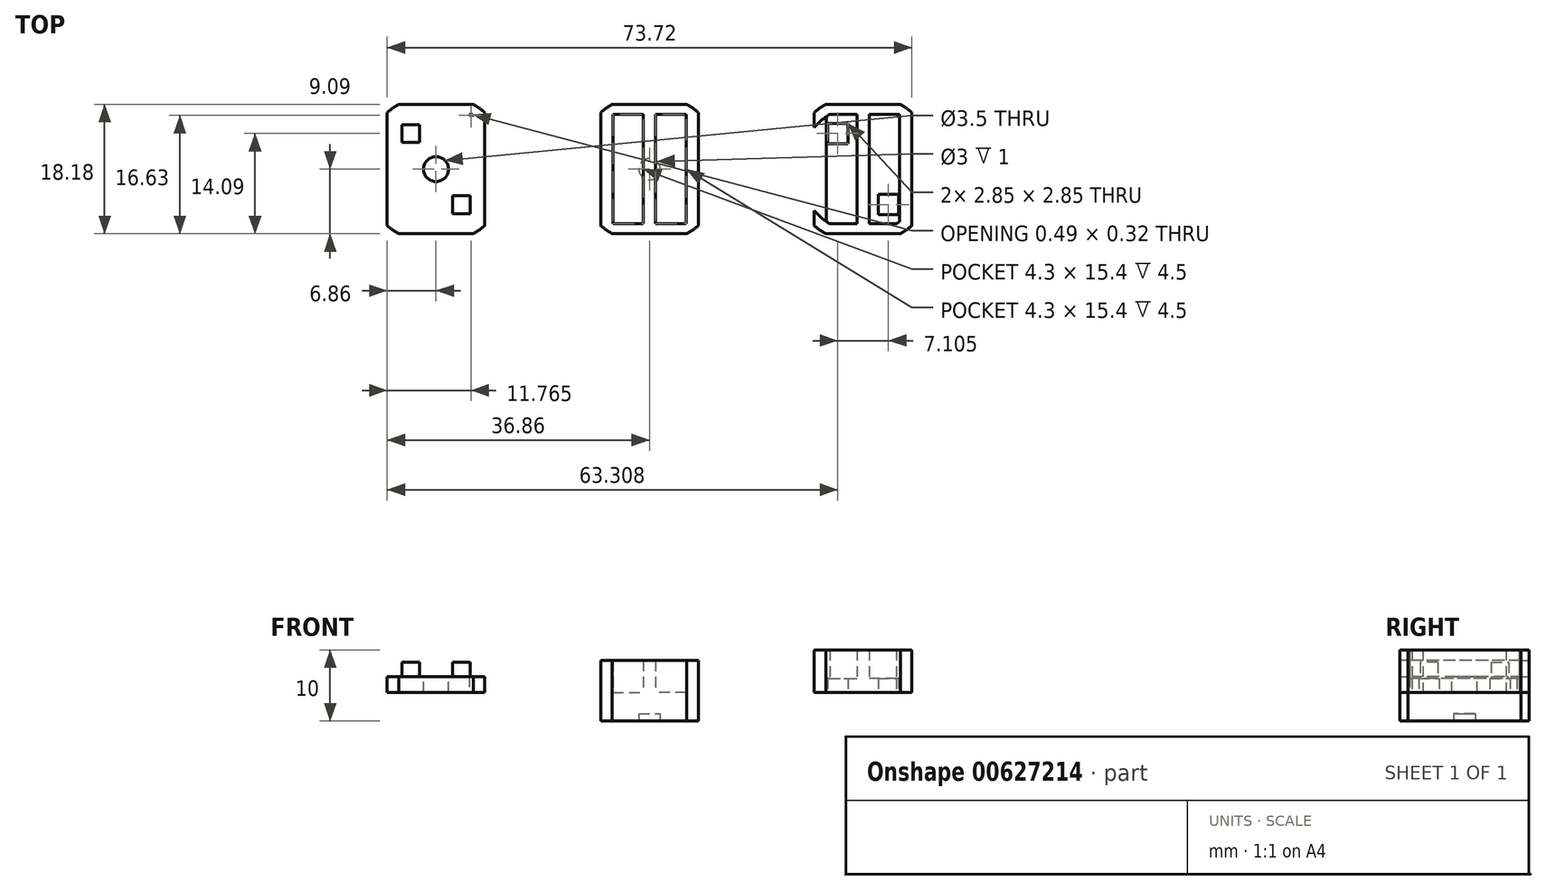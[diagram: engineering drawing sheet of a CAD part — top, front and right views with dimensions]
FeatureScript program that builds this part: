
annotation { "Feature Type Name" : "Feature", "Feature Type Description" : "" }
export const myFeature = defineFeature(function(context is Context, id is Id, definition is map)
    precondition{}
    {
        {
            var Q0;
            Q0=qCreatedBy(makeId("Top.planeOp"),FACE);
            var sketch = newSketch(context, id + "F0", { "sketchPlane" : qUnion([Q0])});
            skCircle(sketch, "E0", {"center": v(0, 0) * mm, "radius": 10.5 * mm});
            skCircle(sketch, "E1", {"center": v(0, 0) * mm, "radius": 9 * mm});
            skLineSegment(sketch, "E2.bottom", {"start": v(-5.15, 7.7) * mm, "end": v(-0.85, 7.7) * mm});
            skLineSegment(sketch, "E2.top", {"start": v(-5.15, -7.7) * mm, "end": v(-0.85, -7.7) * mm});
            skLineSegment(sketch, "E2.left", {"start": v(-5.15, 7.7) * mm, "end": v(-5.15, -7.7) * mm});
            skLineSegment(sketch, "E2.right", {"start": v(-0.85, 7.7) * mm, "end": v(-0.85, -7.7) * mm});
            skPoint(sketch, "E2.middle", {"position": v(-3, 0) * mm});
            skLineSegment(sketch, "E3.MirrorCS", {"start": v(0.85, 7.7) * mm, "end": v(0.85, -7.7) * mm});
            skLineSegment(sketch, "E4.MirrorCS", {"start": v(5.15, 7.7) * mm, "end": v(0.85, 7.7) * mm});
            skLineSegment(sketch, "E5.MirrorCS", {"start": v(5.15, 7.7) * mm, "end": v(5.15, -7.7) * mm});
            skLineSegment(sketch, "E6.MirrorCS", {"start": v(5.15, -7.7) * mm, "end": v(0.85, -7.7) * mm});
            skLineSegment(sketch, "E7", {"start": v(-6.86, 7.95) * mm, "end": v(-6.86, -7.95) * mm});
            skLineSegment(sketch, "E8", {"start": v(-5.25, -9.1) * mm, "end": v(5.25, -9.1) * mm});
            skLineSegment(sketch, "E9.MirrorCS", {"start": v(6.86, 7.95) * mm, "end": v(6.86, -7.95) * mm});
            skLineSegment(sketch, "E10.MirrorCS", {"start": v(5.25, -9.1) * mm, "end": v(-5.25, -9.1) * mm});
            skLineSegment(sketch, "E11.MirrorCS", {"start": v(5.25, 9.1) * mm, "end": v(-5.25, 9.1) * mm});
            skLineSegment(sketch, "E12", {"start": v(-15, 7.95) * mm, "end": v(-15, -7.95) * mm, "construction": true});
            skLineSegment(sketch, "E13", {"start": v(15, 7.95) * mm, "end": v(15, -7.95) * mm, "construction": true});
            skLineSegment(sketch, "E14.MirrorCS", {"start": v(35.25, -9.1) * mm, "end": v(24.75, -9.1) * mm});
            skLineSegment(sketch, "E15.MirrorCS", {"start": v(24.75, -9.1) * mm, "end": v(35.25, -9.1) * mm});
            skLineSegment(sketch, "E16.MirrorCS", {"start": v(30.85, 7.7) * mm, "end": v(30.85, -7.7) * mm});
            skLineSegment(sketch, "E17.MirrorCS", {"start": v(35.15, -7.7) * mm, "end": v(30.85, -7.7) * mm});
            skLineSegment(sketch, "E18.MirrorCS", {"start": v(29.15, 7.7) * mm, "end": v(29.15, -7.7) * mm});
            skLineSegment(sketch, "E19.MirrorCS", {"start": v(36.86, 7.95) * mm, "end": v(36.86, -7.95) * mm});
            skCircle(sketch, "E20.MirrorC", {"center": v(30, 0) * mm, "radius": 10.5 * mm});
            skLineSegment(sketch, "E21.MirrorCS", {"start": v(24.85, 7.7) * mm, "end": v(29.15, 7.7) * mm});
            skCircle(sketch, "E22.MirrorC", {"center": v(30, 0) * mm, "radius": 9 * mm});
            skLineSegment(sketch, "E23.MirrorCS", {"start": v(24.85, 7.7) * mm, "end": v(24.85, -7.7) * mm});
            skLineSegment(sketch, "E24.MirrorCS", {"start": v(35.15, 7.7) * mm, "end": v(35.15, -7.7) * mm});
            skPoint(sketch, "E25.MirrorP", {"position": v(33, 0) * mm});
            skLineSegment(sketch, "E26.MirrorCS", {"start": v(24.75, 9.1) * mm, "end": v(35.25, 9.1) * mm});
            skLineSegment(sketch, "E27.MirrorCS", {"start": v(23.14, 7.95) * mm, "end": v(23.14, -7.95) * mm});
            skLineSegment(sketch, "E28.MirrorCS", {"start": v(35.15, 7.7) * mm, "end": v(30.85, 7.7) * mm});
            skLineSegment(sketch, "E29.MirrorCS", {"start": v(24.85, -7.7) * mm, "end": v(29.15, -7.7) * mm});
            skLineSegment(sketch, "E30.MirrorCS", {"start": v(-24.75, -9.1) * mm, "end": v(-35.25, -9.1) * mm});
            skLineSegment(sketch, "E31.MirrorCS", {"start": v(-35.15, 7.7) * mm, "end": v(-35.15, -7.7) * mm});
            skLineSegment(sketch, "E32.MirrorCS", {"start": v(-30.85, 7.7) * mm, "end": v(-30.85, -7.7) * mm});
            skCircle(sketch, "E33.MirrorC", {"center": v(-30, 0) * mm, "radius": 10.5 * mm});
            skLineSegment(sketch, "E34.MirrorCS", {"start": v(-24.85, -7.7) * mm, "end": v(-29.15, -7.7) * mm});
            skCircle(sketch, "E35.MirrorC", {"center": v(-30, 0) * mm, "radius": 9 * mm});
            skLineSegment(sketch, "E36.MirrorCS", {"start": v(-35.15, 7.7) * mm, "end": v(-30.85, 7.7) * mm});
            skLineSegment(sketch, "E37.MirrorCS", {"start": v(-24.85, 7.7) * mm, "end": v(-24.85, -7.7) * mm});
            skLineSegment(sketch, "E38.MirrorCS", {"start": v(-24.85, 7.7) * mm, "end": v(-29.15, 7.7) * mm});
            skLineSegment(sketch, "E39.MirrorCS", {"start": v(-29.15, 7.7) * mm, "end": v(-29.15, -7.7) * mm});
            skLineSegment(sketch, "E40.MirrorCS", {"start": v(-35.25, 9.1) * mm, "end": v(-24.75, 9.1) * mm});
            skLineSegment(sketch, "E41.MirrorCS", {"start": v(-35.25, -9.1) * mm, "end": v(-24.75, -9.1) * mm});
            skLineSegment(sketch, "E42.MirrorCS", {"start": v(-36.86, 7.95) * mm, "end": v(-36.86, -7.95) * mm});
            skLineSegment(sketch, "E43.MirrorCS", {"start": v(-23.14, 7.95) * mm, "end": v(-23.14, -7.95) * mm});
            skPoint(sketch, "E44.MirrorP", {"position": v(-27, 0) * mm});
            skLineSegment(sketch, "E45.MirrorCS", {"start": v(-35.15, -7.7) * mm, "end": v(-30.85, -7.7) * mm});
            skSolve(sketch);
        }
        {
            var Q0;
            {var subQ0=sQuery(id+"F0.wireOp",EDGE,"E5.MirrorCS");var subQ1=sQuery(id+"F0.wireOp",EDGE,"E1");var subQ2=makeQuery(id+"F0.imprint","INTERSECT",VERTEX,{"disambiguationData":[OD(0.0)],"derivedFrom":[subQ1,subQ0]});Q0=makeQuery(id+"F0.imprint","IMPRINT",FACE,{"disambiguationData":[TD([[makeQuery(id+"F0.imprint","IMPRINT",EDGE,{"disambiguationData":[TD([[subQ2,1.0]])],"derivedFrom":subQ1}),1.0]])]});}
            var Q1;
            {var subQ9=sQuery(id+"F0.wireOp",EDGE,"E11.MirrorCS");Q1=makeQuery(id+"F0.imprint","IMPRINT",FACE,{"disambiguationData":[TD([[makeQuery(id+"F0.imprint","IMPRINT",EDGE,{"derivedFrom":subQ9}),1.0]])]});}
            var Q2;
            {var subQ3=sQuery(id+"F0.wireOp",EDGE,"E2.right");Q2=makeQuery(id+"F0.imprint","IMPRINT",FACE,{"disambiguationData":[TD([[makeQuery(id+"F0.imprint","IMPRINT",EDGE,{"derivedFrom":subQ3}),1.0]])]});}
            var Q3;
            {var subQ0=sQuery(id+"F0.wireOp",EDGE,"E2.left");var subQ1=sQuery(id+"F0.wireOp",EDGE,"E1");var subQ2=makeQuery(id+"F0.imprint","INTERSECT",VERTEX,{"disambiguationData":[OD(0.0)],"derivedFrom":[subQ1,subQ0]});Q3=makeQuery(id+"F0.imprint","IMPRINT",FACE,{"disambiguationData":[TD([[makeQuery(id+"F0.imprint","IMPRINT",EDGE,{"disambiguationData":[TD([[subQ2,-1.0]])],"derivedFrom":subQ1}),1.0]])]});}
            var Q4;
            {var subQ17=sQuery(id+"F0.wireOp",EDGE,"E8");Q4=makeQuery(id+"F0.imprint","IMPRINT",FACE,{"disambiguationData":[TD([[makeQuery(id+"F0.imprint","IMPRINT",EDGE,{"derivedFrom":subQ17}),1.0]])]});}
            extrude(context, id + "F1", {"entities" : qUnion([Q0, Q1, Q2, Q3, Q4]), "depth" : 4.5 * mm, "offsetDistance" : 25 * mm});
        }
        {
            var Q0;
            {var subQ0=sQuery(id+"F0.wireOp",EDGE,"E3.MirrorCS");Q0=makeQuery(id+"F0.imprint","IMPRINT",FACE,{"disambiguationData":[TD([[makeQuery(id+"F0.imprint","IMPRINT",EDGE,{"derivedFrom":subQ0}),1.0]])]});}
            var Q1;
            {var subQ3=sQuery(id+"F0.wireOp",EDGE,"E2.right");Q1=makeQuery(id+"F0.imprint","IMPRINT",FACE,{"disambiguationData":[TD([[makeQuery(id+"F0.imprint","IMPRINT",EDGE,{"derivedFrom":subQ3}),-1.0]])]});}
            var Q2;
            {var subQ3=sQuery(id+"F0.wireOp",EDGE,"E2.right");Q2=makeQuery(id+"F0.imprint","IMPRINT",FACE,{"disambiguationData":[TD([[makeQuery(id+"F0.imprint","IMPRINT",EDGE,{"derivedFrom":subQ3}),1.0]])]});}
            var Q3;
            {var subQ9=sQuery(id+"F0.wireOp",EDGE,"E11.MirrorCS");Q3=makeQuery(id+"F0.imprint","IMPRINT",FACE,{"disambiguationData":[TD([[makeQuery(id+"F0.imprint","IMPRINT",EDGE,{"derivedFrom":subQ9}),1.0]])]});}
            var Q4;
            {var subQ0=sQuery(id+"F0.wireOp",EDGE,"E5.MirrorCS");var subQ1=sQuery(id+"F0.wireOp",EDGE,"E1");var subQ2=makeQuery(id+"F0.imprint","INTERSECT",VERTEX,{"disambiguationData":[OD(0.0)],"derivedFrom":[subQ1,subQ0]});Q4=makeQuery(id+"F0.imprint","IMPRINT",FACE,{"disambiguationData":[TD([[makeQuery(id+"F0.imprint","IMPRINT",EDGE,{"disambiguationData":[TD([[subQ2,1.0]])],"derivedFrom":subQ1}),1.0]])]});}
            var Q5;
            {var subQ0=sQuery(id+"F0.wireOp",EDGE,"E4.MirrorCS");var subQ1=sQuery(id+"F0.wireOp",EDGE,"E1");var subQ2=makeQuery(id+"F0.imprint","INTERSECT",VERTEX,{"derivedFrom":[subQ1,subQ0]});Q5=makeQuery(id+"F0.imprint","IMPRINT",FACE,{"disambiguationData":[TD([[makeQuery(id+"F0.imprint","IMPRINT",EDGE,{"disambiguationData":[TD([[subQ2,1.0]])],"derivedFrom":subQ1}),-1.0]])]});}
            var Q6;
            {var subQ17=sQuery(id+"F0.wireOp",EDGE,"E8");Q6=makeQuery(id+"F0.imprint","IMPRINT",FACE,{"disambiguationData":[TD([[makeQuery(id+"F0.imprint","IMPRINT",EDGE,{"derivedFrom":subQ17}),1.0]])]});}
            var Q7;
            {var subQ0=sQuery(id+"F0.wireOp",EDGE,"E2.left");var subQ1=sQuery(id+"F0.wireOp",EDGE,"E1");var subQ2=makeQuery(id+"F0.imprint","INTERSECT",VERTEX,{"disambiguationData":[OD(0.0)],"derivedFrom":[subQ1,subQ0]});Q7=makeQuery(id+"F0.imprint","IMPRINT",FACE,{"disambiguationData":[TD([[makeQuery(id+"F0.imprint","IMPRINT",EDGE,{"disambiguationData":[TD([[subQ2,-1.0]])],"derivedFrom":subQ1}),1.0]])]});}
            var Q8;
            {var subQ0=sQuery(id+"F0.wireOp",EDGE,"E2.bottom");var subQ1=sQuery(id+"F0.wireOp",EDGE,"E1");var subQ2=makeQuery(id+"F0.imprint","INTERSECT",VERTEX,{"derivedFrom":[subQ1,subQ0]});Q8=makeQuery(id+"F0.imprint","IMPRINT",FACE,{"disambiguationData":[TD([[makeQuery(id+"F0.imprint","IMPRINT",EDGE,{"disambiguationData":[TD([[subQ2,-1.0]])],"derivedFrom":subQ1}),-1.0]])]});}
            var Q9;
            {var subQ0=sQuery(id+"F0.wireOp",EDGE,"E2.top");var subQ1=sQuery(id+"F0.wireOp",EDGE,"E1");var subQ2=makeQuery(id+"F0.imprint","INTERSECT",VERTEX,{"derivedFrom":[subQ1,subQ0]});Q9=makeQuery(id+"F0.imprint","IMPRINT",FACE,{"disambiguationData":[TD([[makeQuery(id+"F0.imprint","IMPRINT",EDGE,{"disambiguationData":[TD([[subQ2,1.0]])],"derivedFrom":subQ1}),-1.0]])]});}
            var Q10;
            {var subQ0=sQuery(id+"F0.wireOp",EDGE,"E6.MirrorCS");var subQ1=sQuery(id+"F0.wireOp",EDGE,"E1");var subQ2=makeQuery(id+"F0.imprint","INTERSECT",VERTEX,{"derivedFrom":[subQ1,subQ0]});Q10=makeQuery(id+"F0.imprint","IMPRINT",FACE,{"disambiguationData":[TD([[makeQuery(id+"F0.imprint","IMPRINT",EDGE,{"disambiguationData":[TD([[subQ2,-1.0]])],"derivedFrom":subQ1}),-1.0]])]});}
            extrude(context, id + "F2", {"entities" : qUnion([Q0, Q1, Q2, Q3, Q4, Q5, Q6, Q7, Q8, Q9, Q10]), "operationType" : NewBodyOperationType.ADD, "oppositeDirection" : true, "depth" : 4 * mm, "offsetDistance" : 25 * mm});
        }
        {
            var Q0;
            Q0=makeQuery(id+"F2.opExtrude","CAP_FACE",FACE,{"disambiguationData":[OSD([sQuery(id+"F0.wireOp",EDGE,"E0"),sQuery(id+"F0.wireOp",EDGE,"E7"),sQuery(id+"F0.wireOp",EDGE,"E8"),sQuery(id+"F0.wireOp",EDGE,"E9.MirrorCS"),sQuery(id+"F0.wireOp",EDGE,"E11.MirrorCS")])],"isStart":false});
            var sketch = newSketch(context, id + "F3", { "sketchPlane" : qUnion([Q0])});
            skCircle(sketch, "E46", {"center": v(0, 0) * mm, "radius": 1.5 * mm});
            skSolve(sketch);
        }
        {
            var Q0;
            Q0=makeQuery(id+"F3.imprint","IMPRINT",FACE,{"disambiguationData":[TD([[makeQuery(id+"F3.imprint","IMPRINT",EDGE,{"derivedFrom":sQuery(id+"F3.wireOp",EDGE,"E46")}),1.0]])]});
            extrude(context, id + "F4", {"entities" : qUnion([Q0]), "operationType" : NewBodyOperationType.REMOVE, "oppositeDirection" : true, "depth" : 1 * mm, "offsetDistance" : 25 * mm});
        }
        {
            var Q0;
            {var subQ0=sQuery(id+"F0.wireOp",EDGE,"E40.MirrorCS");Q0=makeQuery(id+"F0.imprint","IMPRINT",FACE,{"disambiguationData":[TD([[makeQuery(id+"F0.imprint","IMPRINT",EDGE,{"derivedFrom":subQ0}),-1.0]])]});}
            var Q1;
            {var subQ0=sQuery(id+"F0.wireOp",EDGE,"E35.MirrorC");var subQ1=sQuery(id+"F0.wireOp",EDGE,"E31.MirrorCS");var subQ2=makeQuery(id+"F0.imprint","INTERSECT",VERTEX,{"disambiguationData":[OD(0.0)],"derivedFrom":[subQ1,subQ0]});Q1=makeQuery(id+"F0.imprint","IMPRINT",FACE,{"disambiguationData":[TD([[makeQuery(id+"F0.imprint","IMPRINT",EDGE,{"disambiguationData":[TD([[subQ2,-1.0]])],"derivedFrom":subQ1}),-1.0]])]});}
            var Q2;
            {var subQ0=sQuery(id+"F0.wireOp",EDGE,"E35.MirrorC");var subQ1=sQuery(id+"F0.wireOp",EDGE,"E31.MirrorCS");var subQ2=makeQuery(id+"F0.imprint","INTERSECT",VERTEX,{"disambiguationData":[OD(0.0)],"derivedFrom":[subQ1,subQ0]});Q2=makeQuery(id+"F0.imprint","IMPRINT",FACE,{"disambiguationData":[TD([[makeQuery(id+"F0.imprint","IMPRINT",EDGE,{"disambiguationData":[TD([[subQ2,1.0]])],"derivedFrom":subQ1}),1.0]])]});}
            var Q3;
            {var subQ10=sQuery(id+"F0.wireOp",EDGE,"E32.MirrorCS");Q3=makeQuery(id+"F0.imprint","IMPRINT",FACE,{"disambiguationData":[TD([[makeQuery(id+"F0.imprint","IMPRINT",EDGE,{"derivedFrom":subQ10}),1.0]])]});}
            var Q4;
            {var subQ8=sQuery(id+"F0.wireOp",EDGE,"E32.MirrorCS");Q4=makeQuery(id+"F0.imprint","IMPRINT",FACE,{"disambiguationData":[TD([[makeQuery(id+"F0.imprint","IMPRINT",EDGE,{"derivedFrom":subQ8}),-1.0]])]});}
            var Q5;
            {var subQ8=sQuery(id+"F0.wireOp",EDGE,"E39.MirrorCS");Q5=makeQuery(id+"F0.imprint","IMPRINT",FACE,{"disambiguationData":[TD([[makeQuery(id+"F0.imprint","IMPRINT",EDGE,{"derivedFrom":subQ8}),1.0]])]});}
            var Q6;
            {var subQ0=sQuery(id+"F0.wireOp",EDGE,"E37.MirrorCS");var subQ1=sQuery(id+"F0.wireOp",EDGE,"E35.MirrorC");var subQ2=makeQuery(id+"F0.imprint","INTERSECT",VERTEX,{"disambiguationData":[OD(0.0)],"derivedFrom":[subQ1,subQ0]});Q6=makeQuery(id+"F0.imprint","IMPRINT",FACE,{"disambiguationData":[TD([[makeQuery(id+"F0.imprint","IMPRINT",EDGE,{"disambiguationData":[TD([[subQ2,1.0]])],"derivedFrom":subQ1}),1.0]])]});}
            var Q7;
            {var subQ0=sQuery(id+"F0.wireOp",EDGE,"E37.MirrorCS");var subQ1=sQuery(id+"F0.wireOp",EDGE,"E35.MirrorC");var subQ2=makeQuery(id+"F0.imprint","INTERSECT",VERTEX,{"disambiguationData":[OD(1.0)],"derivedFrom":[subQ1,subQ0]});Q7=makeQuery(id+"F0.imprint","IMPRINT",FACE,{"disambiguationData":[TD([[makeQuery(id+"F0.imprint","IMPRINT",EDGE,{"disambiguationData":[TD([[subQ2,1.0]])],"derivedFrom":subQ1}),-1.0]])]});}
            var Q8;
            {var subQ14=sQuery(id+"F0.wireOp",EDGE,"E30.MirrorCS");Q8=makeQuery(id+"F0.imprint","IMPRINT",FACE,{"disambiguationData":[TD([[makeQuery(id+"F0.imprint","IMPRINT",EDGE,{"derivedFrom":subQ14}),-1.0]])]});}
            var Q9;
            {var subQ0=sQuery(id+"F0.wireOp",EDGE,"E35.MirrorC");var subQ1=sQuery(id+"F0.wireOp",EDGE,"E34.MirrorCS");var subQ2=makeQuery(id+"F0.imprint","INTERSECT",VERTEX,{"derivedFrom":[subQ1,subQ0]});Q9=makeQuery(id+"F0.imprint","IMPRINT",FACE,{"disambiguationData":[TD([[makeQuery(id+"F0.imprint","IMPRINT",EDGE,{"disambiguationData":[TD([[subQ2,1.0]])],"derivedFrom":subQ1}),-1.0]])]});}
            var Q10;
            {var subQ0=sQuery(id+"F0.wireOp",EDGE,"E45.MirrorCS");var subQ1=sQuery(id+"F0.wireOp",EDGE,"E31.MirrorCS");var subQ2=makeQuery(id+"F0.imprint","INTERSECT",VERTEX,{"derivedFrom":[subQ1,subQ0]});Q10=makeQuery(id+"F0.imprint","IMPRINT",FACE,{"disambiguationData":[TD([[makeQuery(id+"F0.imprint","IMPRINT",EDGE,{"disambiguationData":[TD([[subQ2,1.0]])],"derivedFrom":subQ1}),1.0]])]});}
            extrude(context, id + "F5", {"entities" : qUnion([Q0, Q1, Q2, Q3, Q4, Q5, Q6, Q7, Q8, Q9, Q10]), "depth" : 2.25 * mm, "offsetDistance" : 25 * mm});
        }
        {
            var Q0;
            Q0=makeQuery(id+"F5.opExtrude","CAP_FACE",FACE,{"disambiguationData":[OSD([sQuery(id+"F0.wireOp",EDGE,"E30.MirrorCS"),sQuery(id+"F0.wireOp",EDGE,"E33.MirrorC"),sQuery(id+"F0.wireOp",EDGE,"E40.MirrorCS"),sQuery(id+"F0.wireOp",EDGE,"E42.MirrorCS"),sQuery(id+"F0.wireOp",EDGE,"E43.MirrorCS")])],"isStart":false});
            var sketch = newSketch(context, id + "F6", { "sketchPlane" : qUnion([Q0])});
            skCircle(sketch, "E47", {"center": v(-30, 0) * mm, "radius": 1.75 * mm});
            skSolve(sketch);
        }
        {
            var Q0;
            Q0 = qSketchRegion(id + "F6", true);
            extrude(context, id + "F7", {"entities" : qUnion([Q0]), "operationType" : NewBodyOperationType.REMOVE, "oppositeDirection" : true, "depth" : 25 * mm, "offsetDistance" : 25 * mm});
        }
        {
            var Q0;
            Q0=makeQuery(id+"F5.opExtrude","CAP_FACE",FACE,{"disambiguationData":[OSD([sQuery(id+"F0.wireOp",EDGE,"E30.MirrorCS"),sQuery(id+"F0.wireOp",EDGE,"E33.MirrorC"),sQuery(id+"F0.wireOp",EDGE,"E40.MirrorCS"),sQuery(id+"F0.wireOp",EDGE,"E42.MirrorCS"),sQuery(id+"F0.wireOp",EDGE,"E43.MirrorCS")])],"isStart":false});
            var sketch = newSketch(context, id + "F8", { "sketchPlane" : qUnion([Q0])});
            skLineSegment(sketch, "E48", {"start": v(-36.08, 8.56) * mm, "end": v(-23.92, -8.56) * mm, "construction": true});
            skLineSegment(sketch, "E49.bottom", {"start": v(-32.3, 3.75) * mm, "end": v(-34.8, 3.75) * mm});
            skLineSegment(sketch, "E49.top", {"start": v(-32.3, 6.25) * mm, "end": v(-34.8, 6.25) * mm});
            skLineSegment(sketch, "E49.left", {"start": v(-32.3, 3.75) * mm, "end": v(-32.3, 6.25) * mm});
            skLineSegment(sketch, "E49.right", {"start": v(-34.8, 3.75) * mm, "end": v(-34.8, 6.25) * mm});
            skPoint(sketch, "E49.middle", {"position": v(-33.55, 5) * mm});
            skLineSegment(sketch, "E50.bottom", {"start": v(-27.7, -3.75) * mm, "end": v(-25.2, -3.75) * mm});
            skLineSegment(sketch, "E50.top", {"start": v(-27.7, -6.25) * mm, "end": v(-25.2, -6.25) * mm});
            skLineSegment(sketch, "E50.left", {"start": v(-27.7, -3.75) * mm, "end": v(-27.7, -6.25) * mm});
            skLineSegment(sketch, "E50.right", {"start": v(-25.2, -3.75) * mm, "end": v(-25.2, -6.25) * mm});
            skPoint(sketch, "E50.middle", {"position": v(-26.45, -5) * mm});
            skSolve(sketch);
        }
        {
            var Q0;
            Q0=makeQuery(id+"F8.imprint","IMPRINT",FACE,{"disambiguationData":[TD([[makeQuery(id+"F8.imprint","IMPRINT",EDGE,{"derivedFrom":sQuery(id+"F8.wireOp",EDGE,"E49.bottom")}),-1.0]])]});
            var Q1;
            Q1=makeQuery(id+"F8.imprint","IMPRINT",FACE,{"disambiguationData":[TD([[makeQuery(id+"F8.imprint","IMPRINT",EDGE,{"derivedFrom":sQuery(id+"F8.wireOp",EDGE,"E50.bottom")}),-1.0]])]});
            extrude(context, id + "F9", {"entities" : qUnion([Q0, Q1]), "operationType" : NewBodyOperationType.ADD, "depth" : 2 * mm, "offsetDistance" : 25 * mm});
        }
        {
            var Q0;
            {var subQ7=sQuery(id+"F0.wireOp",EDGE,"E16.MirrorCS");Q0=makeQuery(id+"F0.imprint","IMPRINT",FACE,{"disambiguationData":[TD([[makeQuery(id+"F0.imprint","IMPRINT",EDGE,{"derivedFrom":subQ7}),-1.0]])]});}
            var Q1;
            {var subQ7=sQuery(id+"F0.wireOp",EDGE,"E14.MirrorCS");Q1=makeQuery(id+"F0.imprint","IMPRINT",FACE,{"disambiguationData":[TD([[makeQuery(id+"F0.imprint","IMPRINT",EDGE,{"derivedFrom":subQ7}),-1.0]])]});}
            var Q2;
            {var subQ0=sQuery(id+"F0.wireOp",EDGE,"E22.MirrorC");var subQ1=sQuery(id+"F0.wireOp",EDGE,"E19.MirrorCS");var subQ2=makeQuery(id+"F0.imprint","INTERSECT",VERTEX,{"disambiguationData":[OD(0.0)],"derivedFrom":[subQ1,subQ0]});Q2=makeQuery(id+"F0.imprint","IMPRINT",FACE,{"disambiguationData":[TD([[makeQuery(id+"F0.imprint","IMPRINT",EDGE,{"disambiguationData":[TD([[subQ2,-1.0]])],"derivedFrom":subQ1}),-1.0]])]});}
            var Q3;
            {var subQ0=sQuery(id+"F0.wireOp",EDGE,"E26.MirrorCS");Q3=makeQuery(id+"F0.imprint","IMPRINT",FACE,{"disambiguationData":[TD([[makeQuery(id+"F0.imprint","IMPRINT",EDGE,{"derivedFrom":subQ0}),-1.0]])]});}
            var Q4;
            {var subQ0=sQuery(id+"F0.wireOp",EDGE,"E23.MirrorCS");var subQ1=sQuery(id+"F0.wireOp",EDGE,"E22.MirrorC");var subQ2=makeQuery(id+"F0.imprint","INTERSECT",VERTEX,{"disambiguationData":[OD(1.0)],"derivedFrom":[subQ1,subQ0]});Q4=makeQuery(id+"F0.imprint","IMPRINT",FACE,{"disambiguationData":[TD([[makeQuery(id+"F0.imprint","IMPRINT",EDGE,{"disambiguationData":[TD([[subQ2,-1.0]])],"derivedFrom":subQ1}),-1.0]])]});}
            var Q5;
            {var subQ0=sQuery(id+"F0.wireOp",EDGE,"E22.MirrorC");var subQ1=sQuery(id+"F0.wireOp",EDGE,"E21.MirrorCS");var subQ2=makeQuery(id+"F0.imprint","INTERSECT",VERTEX,{"derivedFrom":[subQ1,subQ0]});Q5=makeQuery(id+"F0.imprint","IMPRINT",FACE,{"disambiguationData":[TD([[makeQuery(id+"F0.imprint","IMPRINT",EDGE,{"disambiguationData":[TD([[subQ2,1.0]])],"derivedFrom":subQ1}),-1.0]])]});}
            var Q6;
            {var subQ0=sQuery(id+"F0.wireOp",EDGE,"E24.MirrorCS");var subQ1=sQuery(id+"F0.wireOp",EDGE,"E22.MirrorC");var subQ2=makeQuery(id+"F0.imprint","INTERSECT",VERTEX,{"disambiguationData":[OD(0.0)],"derivedFrom":[subQ1,subQ0]});Q6=makeQuery(id+"F0.imprint","IMPRINT",FACE,{"disambiguationData":[TD([[makeQuery(id+"F0.imprint","IMPRINT",EDGE,{"disambiguationData":[TD([[subQ2,1.0]])],"derivedFrom":subQ1}),1.0]])]});}
            var Q7;
            {var subQ0=sQuery(id+"F0.wireOp",EDGE,"E22.MirrorC");var subQ1=sQuery(id+"F0.wireOp",EDGE,"E17.MirrorCS");var subQ2=makeQuery(id+"F0.imprint","INTERSECT",VERTEX,{"derivedFrom":[subQ1,subQ0]});Q7=makeQuery(id+"F0.imprint","IMPRINT",FACE,{"disambiguationData":[TD([[makeQuery(id+"F0.imprint","IMPRINT",EDGE,{"disambiguationData":[TD([[subQ2,1.0]])],"derivedFrom":subQ1}),-1.0]])]});}
            var Q8;
            {var subQ0=sQuery(id+"F0.wireOp",EDGE,"E29.MirrorCS");var subQ1=sQuery(id+"F0.wireOp",EDGE,"E22.MirrorC");var subQ2=makeQuery(id+"F0.imprint","INTERSECT",VERTEX,{"derivedFrom":[subQ1,subQ0]});Q8=makeQuery(id+"F0.imprint","IMPRINT",FACE,{"disambiguationData":[TD([[makeQuery(id+"F0.imprint","IMPRINT",EDGE,{"disambiguationData":[TD([[subQ2,-1.0]])],"derivedFrom":subQ1}),1.0]])]});}
            extrude(context, id + "F10", {"entities" : qUnion([Q0, Q1, Q2, Q3, Q4, Q5, Q6, Q7, Q8]), "depth" : 6 * mm, "offsetDistance" : 25 * mm});
        }
        {
            var Q0;
            {var subQ0=sQuery(id+"F0.wireOp",EDGE,"E23.MirrorCS");var subQ1=sQuery(id+"F0.wireOp",EDGE,"E22.MirrorC");var subQ2=makeQuery(id+"F0.imprint","INTERSECT",VERTEX,{"disambiguationData":[OD(1.0)],"derivedFrom":[subQ1,subQ0]});Q0=makeQuery(id+"F0.imprint","IMPRINT",FACE,{"disambiguationData":[TD([[makeQuery(id+"F0.imprint","IMPRINT",EDGE,{"disambiguationData":[TD([[subQ2,-1.0]])],"derivedFrom":subQ1}),-1.0]])]});}
            var Q1;
            {var subQ8=sQuery(id+"F0.wireOp",EDGE,"E18.MirrorCS");Q1=makeQuery(id+"F0.imprint","IMPRINT",FACE,{"disambiguationData":[TD([[makeQuery(id+"F0.imprint","IMPRINT",EDGE,{"derivedFrom":subQ8}),-1.0]])]});}
            var Q2;
            {var subQ7=sQuery(id+"F0.wireOp",EDGE,"E16.MirrorCS");Q2=makeQuery(id+"F0.imprint","IMPRINT",FACE,{"disambiguationData":[TD([[makeQuery(id+"F0.imprint","IMPRINT",EDGE,{"derivedFrom":subQ7}),-1.0]])]});}
            var Q3;
            {var subQ8=sQuery(id+"F0.wireOp",EDGE,"E16.MirrorCS");Q3=makeQuery(id+"F0.imprint","IMPRINT",FACE,{"disambiguationData":[TD([[makeQuery(id+"F0.imprint","IMPRINT",EDGE,{"derivedFrom":subQ8}),1.0]])]});}
            var Q4;
            {var subQ7=sQuery(id+"F0.wireOp",EDGE,"E14.MirrorCS");Q4=makeQuery(id+"F0.imprint","IMPRINT",FACE,{"disambiguationData":[TD([[makeQuery(id+"F0.imprint","IMPRINT",EDGE,{"derivedFrom":subQ7}),-1.0]])]});}
            var Q5;
            {var subQ0=sQuery(id+"F0.wireOp",EDGE,"E22.MirrorC");var subQ1=sQuery(id+"F0.wireOp",EDGE,"E19.MirrorCS");var subQ2=makeQuery(id+"F0.imprint","INTERSECT",VERTEX,{"disambiguationData":[OD(0.0)],"derivedFrom":[subQ1,subQ0]});Q5=makeQuery(id+"F0.imprint","IMPRINT",FACE,{"disambiguationData":[TD([[makeQuery(id+"F0.imprint","IMPRINT",EDGE,{"disambiguationData":[TD([[subQ2,-1.0]])],"derivedFrom":subQ1}),-1.0]])]});}
            var Q6;
            {var subQ0=sQuery(id+"F0.wireOp",EDGE,"E26.MirrorCS");Q6=makeQuery(id+"F0.imprint","IMPRINT",FACE,{"disambiguationData":[TD([[makeQuery(id+"F0.imprint","IMPRINT",EDGE,{"derivedFrom":subQ0}),-1.0]])]});}
            var Q7;
            {var subQ0=sQuery(id+"F0.wireOp",EDGE,"E24.MirrorCS");var subQ1=sQuery(id+"F0.wireOp",EDGE,"E22.MirrorC");var subQ2=makeQuery(id+"F0.imprint","INTERSECT",VERTEX,{"disambiguationData":[OD(0.0)],"derivedFrom":[subQ1,subQ0]});Q7=makeQuery(id+"F0.imprint","IMPRINT",FACE,{"disambiguationData":[TD([[makeQuery(id+"F0.imprint","IMPRINT",EDGE,{"disambiguationData":[TD([[subQ2,1.0]])],"derivedFrom":subQ1}),1.0]])]});}
            var Q8;
            {var subQ0=sQuery(id+"F0.wireOp",EDGE,"E22.MirrorC");var subQ1=sQuery(id+"F0.wireOp",EDGE,"E21.MirrorCS");var subQ2=makeQuery(id+"F0.imprint","INTERSECT",VERTEX,{"derivedFrom":[subQ1,subQ0]});Q8=makeQuery(id+"F0.imprint","IMPRINT",FACE,{"disambiguationData":[TD([[makeQuery(id+"F0.imprint","IMPRINT",EDGE,{"disambiguationData":[TD([[subQ2,1.0]])],"derivedFrom":subQ1}),-1.0]])]});}
            var Q9;
            {var subQ0=sQuery(id+"F0.wireOp",EDGE,"E29.MirrorCS");var subQ1=sQuery(id+"F0.wireOp",EDGE,"E22.MirrorC");var subQ2=makeQuery(id+"F0.imprint","INTERSECT",VERTEX,{"derivedFrom":[subQ1,subQ0]});Q9=makeQuery(id+"F0.imprint","IMPRINT",FACE,{"disambiguationData":[TD([[makeQuery(id+"F0.imprint","IMPRINT",EDGE,{"disambiguationData":[TD([[subQ2,-1.0]])],"derivedFrom":subQ1}),1.0]])]});}
            var Q10;
            {var subQ0=sQuery(id+"F0.wireOp",EDGE,"E22.MirrorC");var subQ1=sQuery(id+"F0.wireOp",EDGE,"E17.MirrorCS");var subQ2=makeQuery(id+"F0.imprint","INTERSECT",VERTEX,{"derivedFrom":[subQ1,subQ0]});Q10=makeQuery(id+"F0.imprint","IMPRINT",FACE,{"disambiguationData":[TD([[makeQuery(id+"F0.imprint","IMPRINT",EDGE,{"disambiguationData":[TD([[subQ2,1.0]])],"derivedFrom":subQ1}),-1.0]])]});}
            extrude(context, id + "F11", {"entities" : qUnion([Q0, Q1, Q2, Q3, Q4, Q5, Q6, Q7, Q8, Q9, Q10]), "operationType" : NewBodyOperationType.ADD, "depth" : 2 * mm, "offsetDistance" : 25 * mm});
        }
        {
            var Q0;
            {var subQ0=sQuery(id+"F0.wireOp",EDGE,"E27.MirrorCS");var subQ1=sQuery(id+"F0.wireOp",EDGE,"E26.MirrorCS");var subQ2=sQuery(id+"F0.wireOp",EDGE,"E20.MirrorC");var subQ3=sQuery(id+"F0.wireOp",EDGE,"E19.MirrorCS");var subQ4=sQuery(id+"F0.wireOp",EDGE,"E14.MirrorCS");Q0=makeQuery(id+"F11.boolean.opBoolean","MERGE",FACE,{"derivedFrom":[makeQuery(id+"F10.opExtrude","CAP_FACE",FACE,{"disambiguationData":[OSD([subQ4,sQuery(id+"F0.wireOp",EDGE,"E16.MirrorCS"),sQuery(id+"F0.wireOp",EDGE,"E17.MirrorCS"),sQuery(id+"F0.wireOp",EDGE,"E18.MirrorCS"),subQ3,subQ2,sQuery(id+"F0.wireOp",EDGE,"E21.MirrorCS"),sQuery(id+"F0.wireOp",EDGE,"E22.MirrorC"),sQuery(id+"F0.wireOp",EDGE,"E23.MirrorCS"),sQuery(id+"F0.wireOp",EDGE,"E24.MirrorCS"),subQ1,subQ0,sQuery(id+"F0.wireOp",EDGE,"E28.MirrorCS"),sQuery(id+"F0.wireOp",EDGE,"E29.MirrorCS")])],"isStart":true}),makeQuery(id+"F11.opExtrude","CAP_FACE",FACE,{"disambiguationData":[OSD([subQ4,subQ3,subQ2,subQ1,subQ0])],"isStart":true})]});}
            var sketch = newSketch(context, id + "F12", { "sketchPlane" : qUnion([Q0])});
            skLineSegment(sketch, "E51", {"start": v(36.08, 8.56) * mm, "end": v(23.92, -8.56) * mm, "construction": true});
            skLineSegment(sketch, "E52.bottom", {"start": v(27.87, -6.42) * mm, "end": v(25.02, -6.42) * mm});
            skLineSegment(sketch, "E52.top", {"start": v(27.87, -3.57) * mm, "end": v(25.02, -3.57) * mm});
            skLineSegment(sketch, "E52.left", {"start": v(27.87, -6.42) * mm, "end": v(27.87, -3.57) * mm});
            skLineSegment(sketch, "E52.right", {"start": v(25.02, -6.42) * mm, "end": v(25.02, -3.57) * mm});
            skPoint(sketch, "E52.middle", {"position": v(26.45, -5) * mm});
            skLineSegment(sketch, "E53.bottom", {"start": v(34.98, 3.57) * mm, "end": v(32.13, 3.57) * mm});
            skLineSegment(sketch, "E53.top", {"start": v(34.98, 6.42) * mm, "end": v(32.13, 6.42) * mm});
            skLineSegment(sketch, "E53.left", {"start": v(34.98, 3.57) * mm, "end": v(34.98, 6.42) * mm});
            skLineSegment(sketch, "E53.right", {"start": v(32.13, 3.57) * mm, "end": v(32.13, 6.42) * mm});
            skPoint(sketch, "E53.middle", {"position": v(33.55, 5) * mm});
            skSolve(sketch);
        }
        {
            var Q0;
            Q0=makeQuery(id+"F12.imprint","IMPRINT",FACE,{"disambiguationData":[TD([[makeQuery(id+"F12.imprint","IMPRINT",EDGE,{"derivedFrom":sQuery(id+"F12.wireOp",EDGE,"E53.bottom")}),-1.0]])]});
            var Q1;
            Q1=makeQuery(id+"F12.imprint","IMPRINT",FACE,{"disambiguationData":[TD([[makeQuery(id+"F12.imprint","IMPRINT",EDGE,{"derivedFrom":sQuery(id+"F12.wireOp",EDGE,"E52.bottom")}),-1.0]])]});
            extrude(context, id + "F13", {"entities" : qUnion([Q0, Q1]), "operationType" : NewBodyOperationType.REMOVE, "oppositeDirection" : true, "depth" : 25 * mm, "offsetDistance" : 25 * mm});
        }
    });
